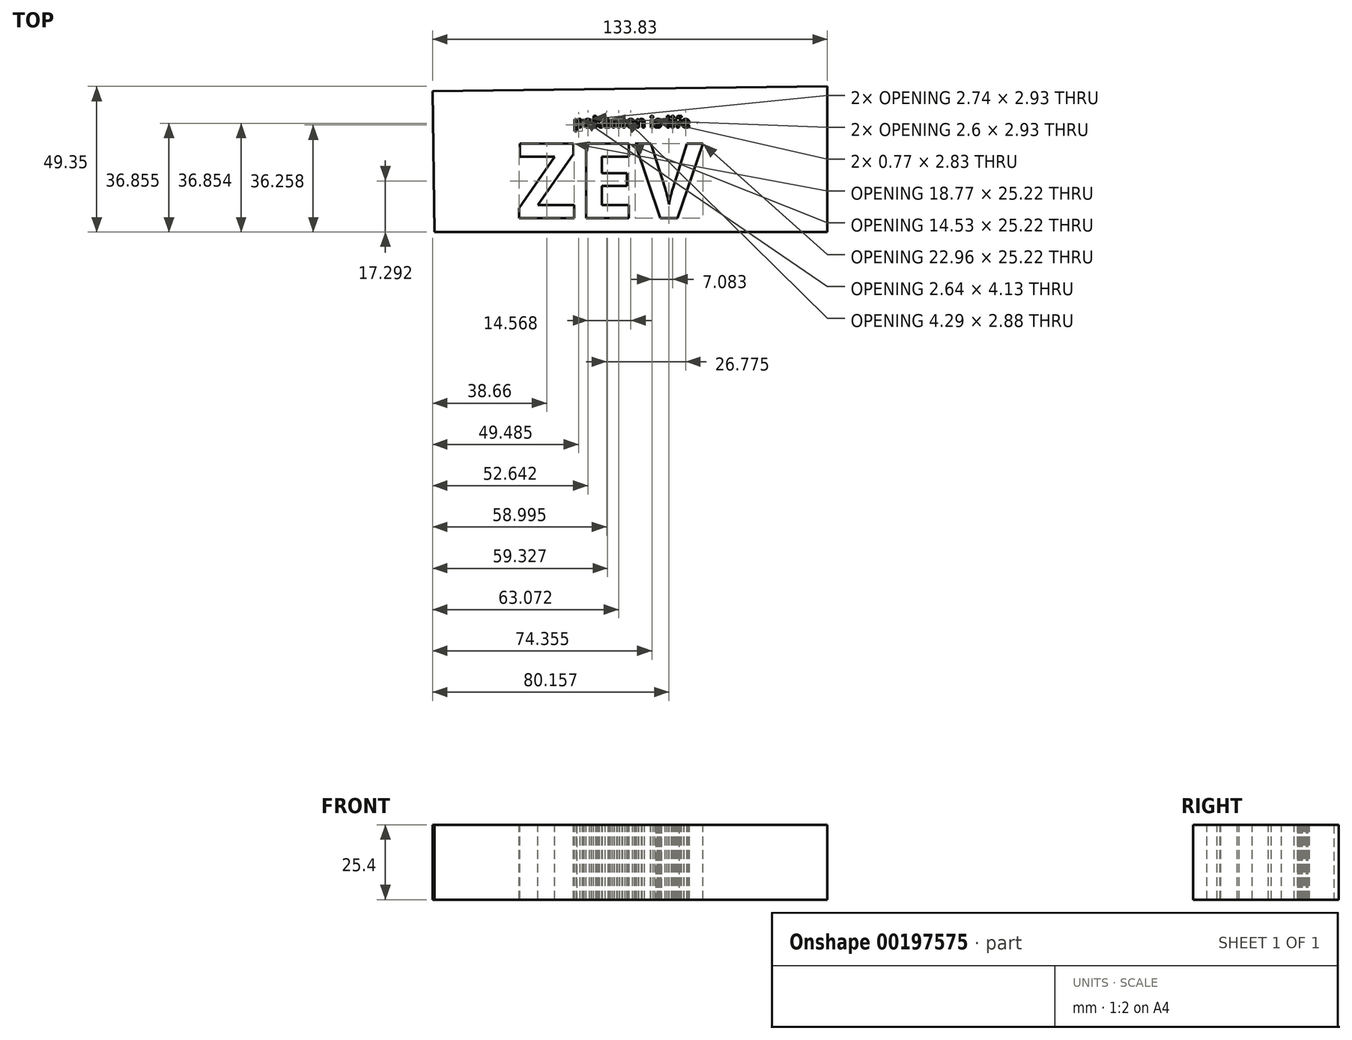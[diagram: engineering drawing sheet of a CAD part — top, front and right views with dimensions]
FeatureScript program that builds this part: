
annotation { "Feature Type Name" : "Feature", "Feature Type Description" : "" }
export const myFeature = defineFeature(function(context is Context, id is Id, definition is map)
    precondition{}
    {
        {
            var Q0;
            Q0=qCreatedBy(makeId("Top.planeOp"),FACE);
            var sketch = newSketch(context, id + "F0", { "sketchPlane" : qUnion([Q0])});
            skLineSegment(sketch, "E0", {"start": v(-65.76, 43) * mm, "end": v(-65.16, -4.68) * mm});
            skLineSegment(sketch, "E1", {"start": v(68.07, -4.68) * mm, "end": v(68.07, 44.67) * mm});
            skLineSegment(sketch, "E2", {"start": v(-65.16, -4.68) * mm, "end": v(68.07, -4.68) * mm});
            skLineSegment(sketch, "E3", {"start": v(-65.76, 43) * mm, "end": v(68.07, 44.67) * mm});
            skSolve(sketch);
        }
        {
            var Q0;
            Q0=makeQuery(id+"F0.imprint","IMPRINT",FACE,{"disambiguationData":[TD([[makeQuery(id+"F0.imprint","IMPRINT",EDGE,{"derivedFrom":sQuery(id+"F0.wireOp",EDGE,"E0")}),1.0]])]});
            extrude(context, id + "F1", {"entities" : qUnion([Q0]), "depth" : 25.4 * mm});
        }
        {
            var Q0;
            Q0=makeQuery(id+"F1.opExtrude","CAP_FACE",FACE,{"disambiguationData":[OSD([sQuery(id+"F0.wireOp",EDGE,"E0"),sQuery(id+"F0.wireOp",EDGE,"UgM4HEvY-U4pS-jpRw-X7Is-Ibp5CuVfuMGr"),sQuery(id+"F0.wireOp",EDGE,"E1"),sQuery(id+"F0.wireOp",EDGE,"OfeVqEn6-ayFk-sWHU-GmTG-yuz35innm4Ju")])],"isStart":false});
            var sketch = newSketch(context, id + "F2", { "sketchPlane" : qUnion([Q0])});
            skText(sketch, "E4", { "text": "ZEV", "fontName": "OpenSans-Bold.ttf"});
            const initialGuessF2  = {"E4": [-0.03733, 0, 1, 0, 0.02544]};
            skSetInitialGuess(sketch, initialGuessF2);
            skSolve(sketch);
        }
        {
            var Q0;
            Q0 = qSketchRegion(id + "F2", true);
            extrude(context, id + "F3", {"entities" : qUnion([Q0]), "operationType" : NewBodyOperationType.REMOVE, "oppositeDirection" : true, "depth" : 25.4 * mm});
        }
        {
            var Q0;
            Q0=makeQuery(id+"F1.opExtrude","CAP_FACE",FACE,{"disambiguationData":[OSD([sQuery(id+"F0.wireOp",EDGE,"E0"),sQuery(id+"F0.wireOp",EDGE,"UgM4HEvY-U4pS-jpRw-X7Is-Ibp5CuVfuMGr"),sQuery(id+"F0.wireOp",EDGE,"E1"),sQuery(id+"F0.wireOp",EDGE,"OfeVqEn6-ayFk-sWHU-GmTG-yuz35innm4Ju")])],"isStart":false});
            var sketch = newSketch(context, id + "F4", { "sketchPlane" : qUnion([Q0])});
            skText(sketch, "E5", { "text": "pokemon is life", "fontName": "OpenSans-Bold.ttf"});
            const initialGuessF4  = {"E5": [-0.018, 0.03076, 1, 0, 0.00373]};
            skSetInitialGuess(sketch, initialGuessF4);
            skSolve(sketch);
        }
        {
            var Q0;
            Q0 = qSketchRegion(id + "F4", true);
            extrude(context, id + "F5", {"entities" : qUnion([Q0]), "operationType" : NewBodyOperationType.REMOVE, "oppositeDirection" : true, "depth" : 25.4 * mm});
        }
    });
